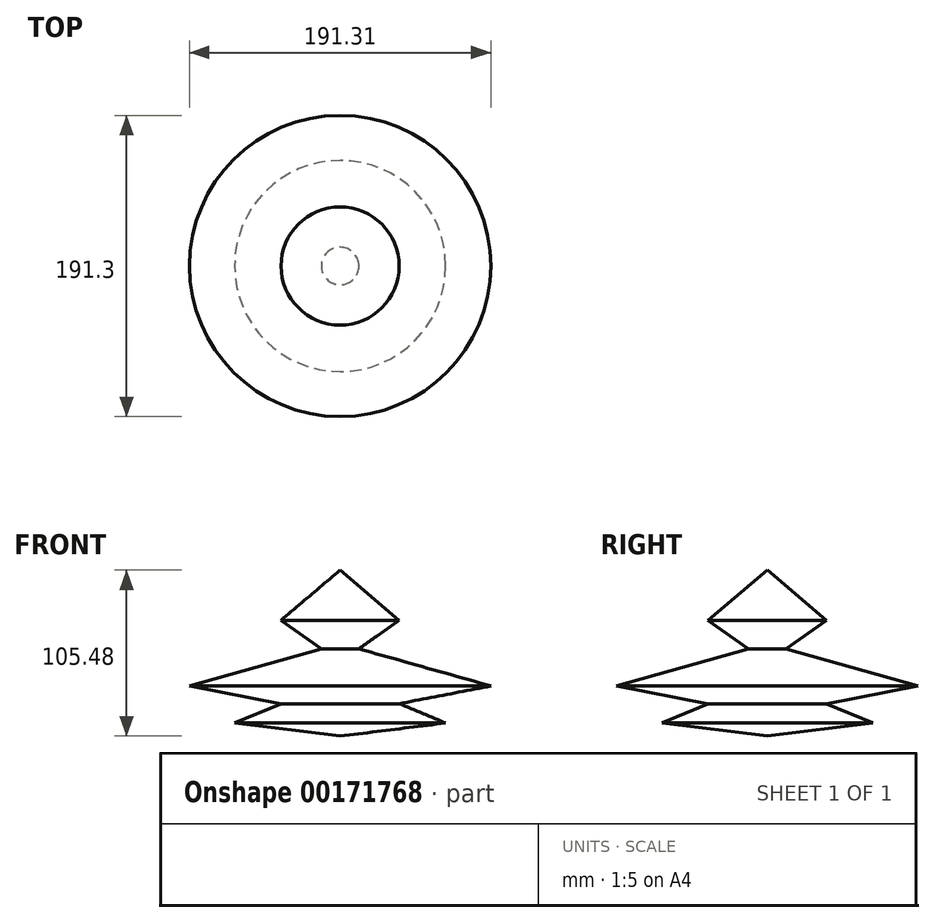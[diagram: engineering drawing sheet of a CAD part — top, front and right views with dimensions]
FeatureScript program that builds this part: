
annotation { "Feature Type Name" : "Feature", "Feature Type Description" : "" }
export const myFeature = defineFeature(function(context is Context, id is Id, definition is map)
    precondition{}
    {
        {
            var Q0;
            Q0=qCreatedBy(makeId("Front.planeOp"),FACE);
            var sketch = newSketch(context, id + "F0", { "sketchPlane" : qUnion([Q0])});
            skLineSegment(sketch, "E0", {"start": v(-48.42, 55.57) * mm, "end": v(-48.42, -49.91) * mm});
            skLineSegment(sketch, "E1", {"start": v(-48.42, 55.57) * mm, "end": v(-10.88, 23.7) * mm});
            skLineSegment(sketch, "E2", {"start": v(-10.88, 23.7) * mm, "end": v(-36.5, 5.51) * mm});
            skLineSegment(sketch, "E3", {"start": v(-36.5, 5.51) * mm, "end": v(47.23, -18.03) * mm});
            skLineSegment(sketch, "E4", {"start": v(47.23, -18.03) * mm, "end": v(-10.88, -29.35) * mm});
            skLineSegment(sketch, "E5", {"start": v(-10.88, -29.35) * mm, "end": v(18.62, -41.57) * mm});
            skLineSegment(sketch, "E6", {"start": v(18.62, -41.57) * mm, "end": v(-48.42, -49.91) * mm});
            skSolve(sketch);
        }
        {
            var Q0;
            Q0=makeQuery(id+"F0.imprint","IMPRINT",FACE,{"disambiguationData":[TD([[makeQuery(id+"F0.imprint","IMPRINT",EDGE,{"derivedFrom":sQuery(id+"F0.wireOp",EDGE,"E0")}),1.0]])]});
            var Q1;
            Q1=sQuery(id+"F0.wireOp",EDGE,"E0");
            revolve(context, id + "F1", {"entities" : qUnion([Q0]), "axis" : qUnion([Q1]), "revolveType" : RevolveType.FULL});
        }
    });
